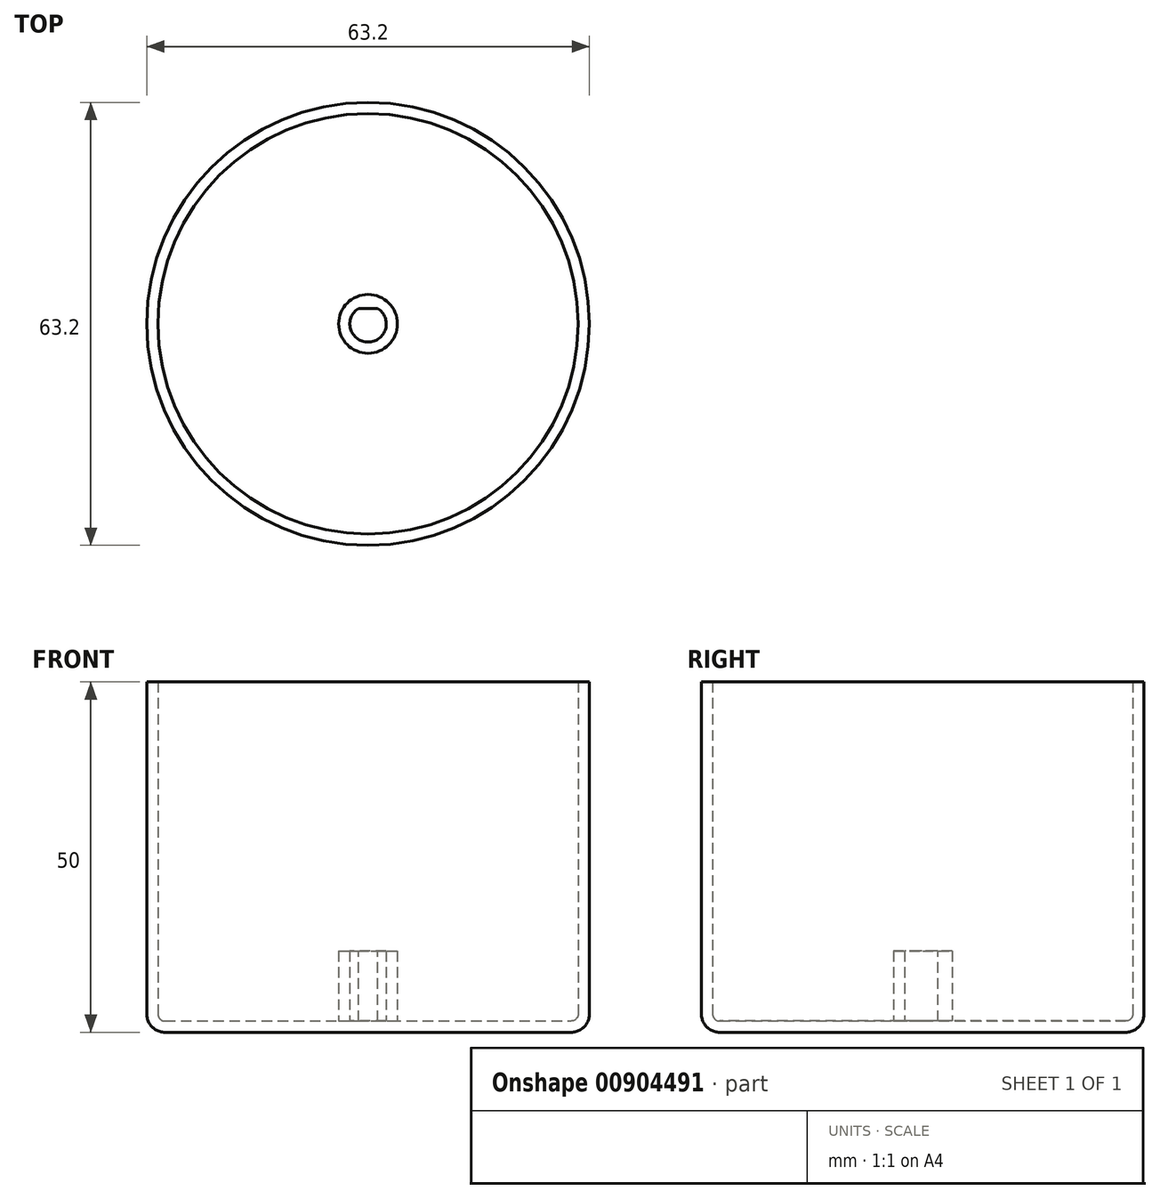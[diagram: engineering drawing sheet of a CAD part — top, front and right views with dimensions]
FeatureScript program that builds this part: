
annotation { "Feature Type Name" : "Feature", "Feature Type Description" : "" }
export const myFeature = defineFeature(function(context is Context, id is Id, definition is map)
    precondition{}
    {
        {
            var Q0;
            Q0=qCreatedBy(makeId("Right.planeOp"),FACE);
            var sketch = newSketch(context, id + "F0", { "sketchPlane" : qUnion([Q0])});
            skLineSegment(sketch, "E0", {"start": v(0, 0) * mm, "end": v(0, 1.6) * mm});
            skLineSegment(sketch, "E1", {"start": v(0, 1.6) * mm, "end": v(2.6, 1.6) * mm});
            skLineSegment(sketch, "E2", {"start": v(2.6, 1.6) * mm, "end": v(2.6, 11.6) * mm});
            skLineSegment(sketch, "E3", {"start": v(2.6, 11.6) * mm, "end": v(4.2, 11.6) * mm});
            skLineSegment(sketch, "E4", {"start": v(4.2, 11.6) * mm, "end": v(4.2, 1.6) * mm});
            skLineSegment(sketch, "E5", {"start": v(4.2, 1.6) * mm, "end": v(29, 1.6) * mm});
            skLineSegment(sketch, "E6", {"start": v(30, 2.6) * mm, "end": v(30, 50) * mm});
            skLineSegment(sketch, "E7", {"start": v(30, 50) * mm, "end": v(31.6, 50) * mm});
            skLineSegment(sketch, "E8", {"start": v(31.6, 50) * mm, "end": v(31.6, 2.6) * mm});
            skLineSegment(sketch, "E9", {"start": v(29, 0) * mm, "end": v(0, 0) * mm});
            skPoint(sketch, "E10.visualSharp", {"position": v(30, 1.6) * mm});
            skArc(sketch, "E10.filletArc", {"start": v(29, 1.6) * mm, "mid": v(29.7, 1.9) * mm, "end": v(30, 2.6) * mm});
            skPoint(sketch, "E11.visualSharp", {"position": v(31.6, 0) * mm});
            skArc(sketch, "E11.filletArc", {"start": v(29, 0) * mm, "mid": v(30.84, 0.76) * mm, "end": v(31.6, 2.6) * mm});
            skSolve(sketch);
        }
        {
            var Q0;
            Q0 = qSketchRegion(id + "F0", true);
            var Q1;
            Q1=sQuery(id+"F0.wireOp",EDGE,"E0");
            revolve(context, id + "F1", {"surfaceOperationType" : NewSurfaceOperationType.NEW, "entities" : qUnion([Q0]), "axis" : qUnion([Q1]), "revolveType" : RevolveType.FULL});
        }
        {
            var Q0;
            Q0=makeQuery(id+"F1.opRevolve","SWEPT_FACE",FACE,{"disambiguationData":[OSD([sQuery(id+"F0.wireOp",EDGE,"E3")])]});
            var sketch = newSketch(context, id + "F2", { "sketchPlane" : qUnion([Q0])});
            skLineSegment(sketch, "E12", {"start": v(-1.39, 2.2) * mm, "end": v(1.39, 2.2) * mm});
            skArc(sketch, "E13", {"start": v(1.39, 2.2) * mm, "mid": v(0, 2.6) * mm, "end": v(-1.39, 2.2) * mm});
            skLineSegment(sketch, "E14", {"start": v(0, 2.2) * mm, "end": v(0, -2.6) * mm, "construction": true});
            skSolve(sketch);
        }
        {
            var Q0;
            Q0=makeQuery(id+"F2.imprint","IMPRINT",FACE,{"disambiguationData":[TD([[makeQuery(id+"F2.imprint","IMPRINT",EDGE,{"derivedFrom":sQuery(id+"F2.wireOp",EDGE,"E12")}),1.0]])]});
            extrude(context, id + "F3", {"entities" : qUnion([Q0]), "operationType" : NewBodyOperationType.ADD, "endBound" : BoundingType.UP_TO_NEXT, "oppositeDirection" : true, "depth" : 25 * mm, "offsetDistance" : 25 * mm});
        }
    });
